# Revit family: P190780JX-032c_JMC6224HM_Urban_Living_Small-Speed-Oven
name_source: partatom
category: Specialty Equipment
units: mm (PartAtom-declared; Revit-internal decimal feet)

## family parameters
Always vertical = Yes
Cut with Voids When Loaded = No
Enable Cutting in Views = No
Maintain Annotation Orientation = No
Part Type = Normal
Room Calculation Point = No
Round Connector Dimension = Use Diameter
Shared = No
Work Plane-Based = No

## types (1)
- JMC6224HM
    Amps = 0 A
    Body Material = ARCAT - Metal - Steel - Stainless
    Clearance Material = ARCAT - Clearance
    Default Elevation = 0"
    Depth = 21 7/8"
    Description = JennAir® NOIR 60cm Built-In Speed Oven
    Dimension Guide = https://www.whirlpool.com
    Display Panel Material = ARCAT - Glass - Tempered - Black
    Door Material = ARCAT - Glass - Tempered - Black
    Family Name = SMALL SPACES - 24" - Small Speed Oven
    Feature 1 = SPEED OVEN
    Feature 2 = 3.5-Inch Full-Color LCD Display
    Feature 3 = Emotive Controls
    Glass Material = ARCAT - Glass - Gray
    Handle Material = ARCAT - Metal - Steel - Gray
    Height = 18 5/16"
    Installation-Fabrication = https://www.whirlpool.com
    Leg Material = ARCAT - Plastic - Black
    Manufacturer = Jenn Air
    Model = JMC6224HM
    Voltage = 0 V
    Width = 23 7/16"

## geometry (parser evidence)
native form markers: Sweep x2
no freeform markers — native parametric forms only
